# Revit family: DCST_Счетчик водяной промышленный_СТВХ «СТРИМ»
name_source: partatom
category: Арматура трубопроводов
units: mm (PartAtom-declared; Revit-internal decimal feet)

## family parameters
Всегда вертикально = Да
На основе рабочей плоскости = Нет
Общий = Нет
При загрузке вырезать с полостями = Нет
Размер круглого соединителя = Использовать диаметр
Тип детали = Вставляется

## types (6) — shared parameters
ADSK_Единица измерения = шт.
ADSK_Завод-изготовитель = Декаст
ADSK_Количество = 1
ADSK_Материал = Декаст_Корпус счетчика синий
LT = СТВХ СТРИМ
R = 20 мм
URL = https://www.decast.com
ИПД_LoRaWAN = ♦ : LoRaWAN
ИПД_ДГ2 = ♦ : импульсный выход (геркон)
ИПД_Коллектор = ♦ : импульсный выход (открытый коллектор)
ИПД_Нет = ♦ : нет
Изготовитель = Декаст

## per-type parameters (varying)
- СТВХ-50 "СТРИМ": ADSK_Диаметр условный=50 мм; D=86.5 мм; D1=98.1 мм; D11=98.1 мм; D12=80.683 мм; D2=60 мм; D3=66 мм; D4=162 мм; D5=130 мм; L1=50 мм; L2=50 мм; W=121.5 мм; X=100 мм; f=22 мм; h1=56 мм; h2=48.3 мм; h3=19.3 мм; h4=15.4 мм; h5=24 мм; hm=128.2 мм; u=15.00°; Диаметр условного прохода=50 мм; Монтажная длина=200 мм; Патрубок_100м=Да; Патрубок_100п=Нет; УГО_Высота=78 мм; УГО_Длина=156 мм; УГО_Длина линии=22 мм
- СТВХ-65 "СТРИМ": ADSK_Диаметр условный=65 мм; D=86.5 мм; D1=98.1 мм; D11=98.1 мм; D12=80.683 мм; D2=78 мм; D3=85.8 мм; D4=162 мм; D5=130 мм; L1=50 мм; L2=50 мм; W=121.5 мм; X=100 мм; f=24 мм; h1=56 мм; h2=48.3 мм; h3=19.3 мм; h4=15.4 мм; h5=24 мм; hm=128.2 мм; u=15.00°; Диаметр условного прохода=65 мм; Монтажная длина=200 мм; Патрубок_100м=Да; Патрубок_100п=Нет; УГО_Высота=76 мм; УГО_Длина=152 мм; УГО_Длина линии=24 мм
- СТВХ-80 "СТРИМ": ADSK_Диаметр условный=80 мм; D=126 мм; D1=116 мм; D11=89 мм; D12=76.093 мм; D2=100 мм; D3=110 мм; D4=162 мм; D5=130 мм; L1=50 мм; L2=50 мм; W=135.5 мм; X=112.5 мм; f=24 мм; h1=92 мм; h2=57 мм; h3=18 мм; h4=11.8 мм; h5=15.4 мм; hm=160 мм; u=11.00°; Диаметр условного прохода=80 мм; Монтажная длина=225 мм; Патрубок_100м=Да; Патрубок_100п=Нет; УГО_Высота=88.5 мм; УГО_Длина=177 мм; УГО_Длина линии=24 мм
- СТВХ-100 "СТРИМ": ADSK_Диаметр условный=100 мм; D=129.5 мм; D1=116 мм; D11=89 мм; D12=76.326 мм; D2=120 мм; D3=120 мм; D4=162 мм; D5=130 мм; L1=50 мм; L2=50 мм; W=140 мм; X=125 мм; f=26 мм; h1=96 мм; h2=65 мм; h3=18 мм; h4=11.8 мм; h5=16 мм; hm=163.4 мм; u=11.00°; Диаметр условного прохода=100 мм; Монтажная длина=250 мм; Патрубок_100м=Да; Патрубок_100п=Нет; УГО_Высота=99 мм; УГО_Длина=198 мм; УГО_Длина линии=26 мм
- СТВХ-150 "СТРИМ": ADSK_Диаметр условный=150 мм; D=105 мм; D1=98 мм; D11=78 мм; D12=61.429 мм; D2=114 мм; D3=114 мм; D4=162 мм; D5=130 мм; L1=50 мм; L2=50 мм; W=115 мм; X=150 мм; f=28 мм; h1=85.5 мм; h2=55 мм; h3=15 мм; h4=11.8 мм; h5=15.8 мм; hm=142.8 мм; u=18.00°; Диаметр условного прохода=150 мм; Монтажная длина=300 мм; Патрубок_100м=Нет; Патрубок_100п=Да; УГО_Высота=122 мм; УГО_Длина=244 мм; УГО_Длина линии=28 мм
- СТВХ-200 "СТРИМ": ADSK_Диаметр условный=200 мм; D=112 мм; D1=116 мм; D11=89 мм; D12=67.815 мм; D2=190 мм; D3=190 мм; D4=225 мм; D5=190 мм; L1=52 мм; L2=75 мм; W=137.5 мм; X=148 мм; f=30 мм; h1=109 мм; h2=90 мм; h3=19.6 мм; h4=11.8 мм; h5=15.8 мм; hm=178 мм; u=18.00°; Диаметр условного прохода=200 мм; Монтажная длина=350 мм; Патрубок_100м=Нет; Патрубок_100п=Да; УГО_Высота=145 мм; УГО_Длина=290 мм; УГО_Длина линии=30 мм
